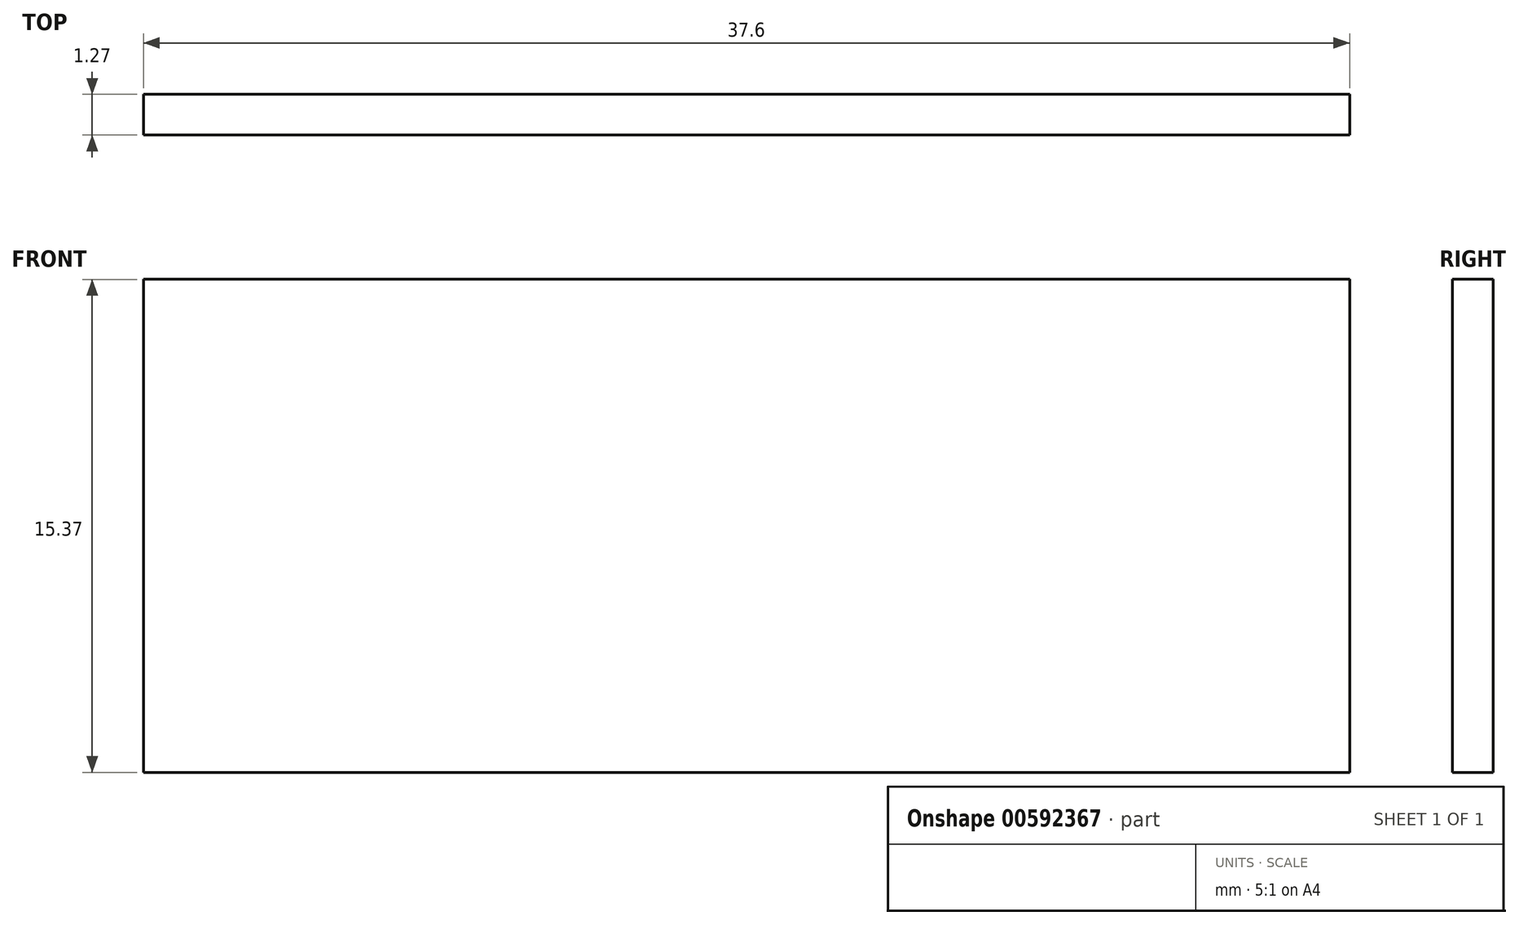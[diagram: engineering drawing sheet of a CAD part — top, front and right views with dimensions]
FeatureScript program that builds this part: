
annotation { "Feature Type Name" : "Feature", "Feature Type Description" : "" }
export const myFeature = defineFeature(function(context is Context, id is Id, definition is map)
    precondition{}
    {
        {
            var Q0;
            Q0=qCreatedBy(makeId("Front.planeOp"),FACE);
            var sketch = newSketch(context, id + "F0", { "sketchPlane" : qUnion([Q0])});
            skLineSegment(sketch, "E0", {"start": v(53.65, 43.55) * mm, "end": v(53.65, 28.18) * mm});
            skLineSegment(sketch, "E1", {"start": v(53.65, 43.55) * mm, "end": v(16.05, 43.55) * mm});
            skLineSegment(sketch, "E2", {"start": v(16.05, 43.55) * mm, "end": v(16.05, 28.18) * mm});
            skLineSegment(sketch, "E3", {"start": v(16.05, 28.18) * mm, "end": v(53.65, 28.18) * mm});
            skSolve(sketch);
        }
        {
            var Q0;
            Q0 = qSketchRegion(id + "F0", true);
            extrude(context, id + "F1", {"entities" : qUnion([Q0]), "depth" : 1.27 * mm, "offsetDistance" : 25.4 * mm});
        }
    });
